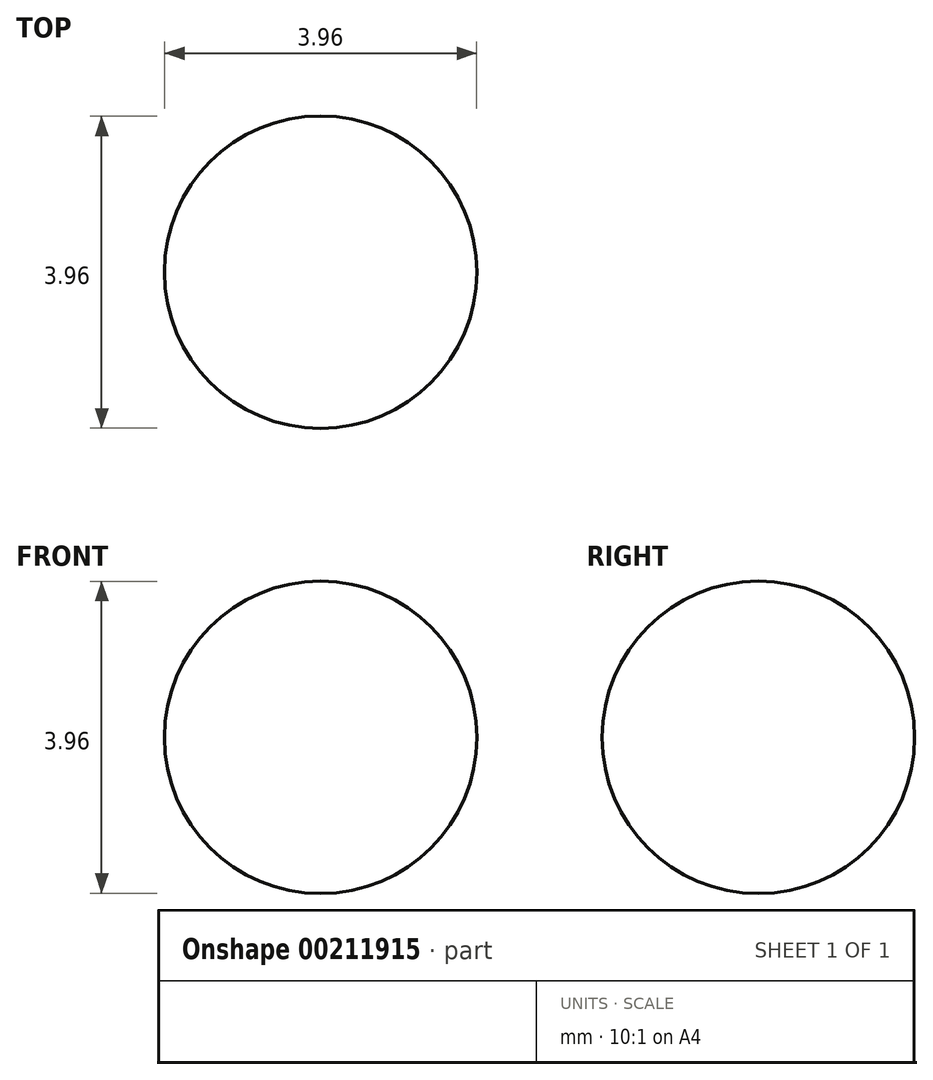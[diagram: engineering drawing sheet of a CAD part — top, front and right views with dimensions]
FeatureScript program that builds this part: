
annotation { "Feature Type Name" : "Feature", "Feature Type Description" : "" }
export const myFeature = defineFeature(function(context is Context, id is Id, definition is map)
    precondition{}
    {
        {
            var Q0;
            Q0=qCreatedBy(makeId("Front.planeOp"),FACE);
            var sketch = newSketch(context, id + "F0", { "sketchPlane" : qUnion([Q0])});
            skArc(sketch, "E0", {"start": v(0, -1.98) * mm, "mid": v(1.98, 0) * mm, "end": v(0, 1.98) * mm});
            skLineSegment(sketch, "E1", {"start": v(0, 1.98) * mm, "end": v(0, -1.98) * mm});
            skSolve(sketch);
        }
        {
            var Q0;
            Q0=makeQuery(id+"F0.imprint","IMPRINT",FACE,{"disambiguationData":[TD([[makeQuery(id+"F0.imprint","IMPRINT",EDGE,{"derivedFrom":sQuery(id+"F0.wireOp",EDGE,"E0")}),1.0]])]});
            var Q1;
            Q1=sQuery(id+"F0.wireOp",EDGE,"E1");
            revolve(context, id + "F1", {"entities" : qUnion([Q0]), "axis" : qUnion([Q1]), "revolveType" : RevolveType.FULL});
        }
    });
